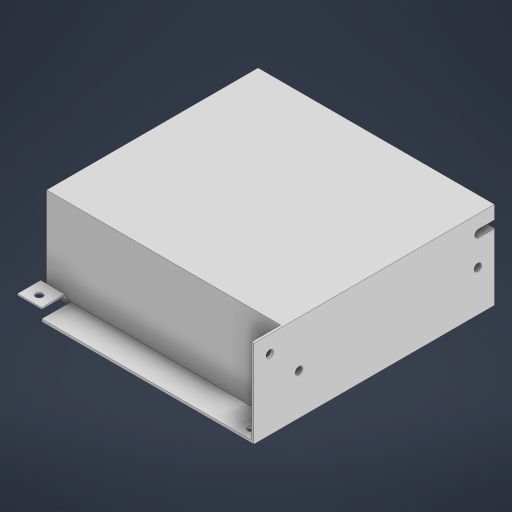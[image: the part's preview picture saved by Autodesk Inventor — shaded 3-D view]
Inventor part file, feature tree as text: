
AUTODESK INVENTOR PART (.ipt)
format: ipt  version: 2024 (Build 280153000, 153)  size: 241,152 bytes
history: native  units: mm
features: extrude x9, sketch x5, chamfer x2, other x1
ambient origin geometry x8: Origin, YZ Plane, XZ Plane, XY Plane, X Axis, Y Axis, Z Axis, Center Point
bodies: Body1 (feature_tree)
feature tree (17):
  other  "솔리드1"
  sketch  "스케치1"
  extrude  "돌출1"  Depth=97.5mm
  extrude  "돌출2"  Depth=99.2mm
  sketch  "스케치2"
  extrude  "돌출3"  Depth=96.5mm
  extrude  "돌출4"  Depth=12.0mm
  extrude  "돌출5"  Depth=1.0mm
  extrude  "돌출6"  Depth=36.0mm TaperAngle=0.0deg
  chamfer  "모따기1"  Distance=1.0mm
  chamfer  "모따기2"  Distance=3.0mm
  sketch  "스케치4"
  extrude  "돌출7"  Depth=5.0mm
  extrude  "돌출8"  Depth=4.0mm
  extrude  "돌출9"  Depth=10.0mm
  sketch  "스케치3"
  sketch  "스케치5"
